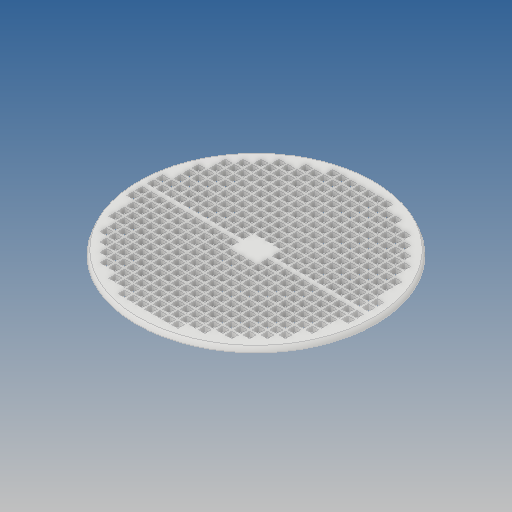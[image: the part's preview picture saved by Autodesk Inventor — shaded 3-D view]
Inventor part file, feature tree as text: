
AUTODESK INVENTOR PART (.ipt)
format: ipt  version: 2020 (Build 240168000, 168)  size: 2,493,440 bytes
history: native  units: mm
features: extrude x24, sketch x24, pattern_linear x6, other x4, projected_geometry x3, mirror x2, revolve x1, loft x1, shell x1
ambient origin geometry x8: Origin, YZ Plane, XZ Plane, XY Plane, X Axis, Y Axis, Z Axis, Center Point
bodies: Body1 (feature_tree)
feature tree (66):
  other  "полочка"
  revolve  "Вращение3"
  extrude  "Выдавливание103"  Depth=170.0mm
  extrude  "Выдавливание104"  Depth=100.0mm
  mirror  "Зеркальное отражение8"
  sketch  "Эскиз121"
  extrude  "Выдавливание105"  Depth=17.0mm
  extrude  "Выдавливание106"  Depth=4.0mm
  extrude  "Выдавливание107"  Depth=35.0mm
  sketch  "Эскиз4"
  other  "РабПлоскость1"
  sketch  "Эскиз5"
  loft  "Лофт1"
  extrude  "Выдавливание2"  TaperAngle=0.0deg  [1 undecoded]
  shell  "Оболочка1"  Thickness=0.0mm
  sketch  "Эскиз21"
  extrude  "Выдавливание16"  Depth=130.0mm TaperAngle=0.0deg
  other  "РабПлоскость7"
  sketch  "Эскиз23"
  extrude  "Выдавливание17"  Depth=5.0mm
  extrude  "Выдавливание18"  Depth=2.0mm
  extrude  "Выдавливание22"  Depth=2.0mm
  extrude  "Выдавливание24"  Depth=10.0mm TaperAngle=0.0deg
  extrude  "Выдавливание25"  Depth=143.802871mm
  pattern_linear  "Прямоуг.массив1"  Spacing1=0.0mm  [1 undecoded]
  pattern_linear  "Прямоуг.массив2"  Spacing1=1.0mm  [1 undecoded]
  extrude  "Выдавливание26"  Depth=30.0mm
  pattern_linear  "Прямоуг.массив3"  Spacing1=2.0mm  [1 undecoded]
  extrude  "Выдавливание27"  Depth=1.0mm TaperAngle=0.0deg
  pattern_linear  "Прямоуг.массив4"  Spacing1=14.0mm  [1 undecoded]
  extrude  "Выдавливание28"  Depth=14.0mm
  pattern_linear  "Прямоуг.массив5"  Spacing1=7.0mm  [1 undecoded]
  extrude  "Выдавливание29"  Depth=10.0mm
  pattern_linear  "Прямоуг.массив6"  Spacing1=3.0mm  [1 undecoded]
  mirror  "Зеркальное отражение7"
  extrude  "Выдавливание95"  Depth=3.0mm
  extrude  "Выдавливание96"  Depth=1.0mm TaperAngle=0.0deg
  extrude  "Выдавливание97"  Depth=14.0mm
  sketch  "Эскиз112"
  extrude  "Выдавливание98"  Depth=14.0mm
  extrude  "Выдавливание99"  Depth=3.0mm
  extrude  "Выдавливание100"  Depth=2.0mm
  extrude  "Выдавливание101"  Depth=7.0mm
  extrude  "Выдавливание102"  Depth=10.0mm
  sketch  "Эскиз6"
  projected_geometry  "Спроецированная петля1"
  sketch  "Эскиз26"
  sketch  "Эскиз28"
  sketch  "Эскиз29"
  sketch  "Эскиз30"
  sketch  "Эскиз31"
  sketch  "Эскиз32"
  sketch  "Эскиз33"
  sketch  "Эскиз109"
  sketch  "Эскиз110"
  sketch  "Эскиз111"
  projected_geometry  "Спроецированная петля42"
  sketch  "Эскиз114"
  projected_geometry  "Спроецированная петля43"
  sketch  "Эскиз115"
  sketch  "Эскиз116"
  sketch  "Эскиз118"
  other  "Твердое тело3"
  sketch  "Эскиз119"
  sketch  "Эскиз120"
  sketch  "Эскиз122"
note: 7 required parameter values undecoded (feature->parameter linkage not recoverable at this tier; creation-order binding heuristic only, values carry confidence <= 0.55)
